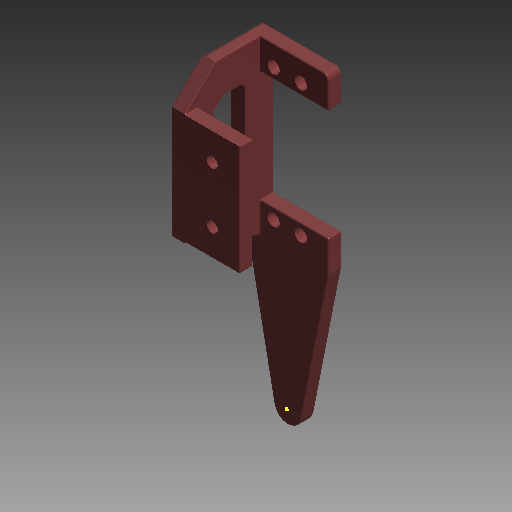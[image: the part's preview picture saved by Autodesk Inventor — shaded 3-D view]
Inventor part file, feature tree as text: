
AUTODESK INVENTOR PART (.ipt)
format: ipt  version: 2017 (Build 210142000, 142)  size: 246,272 bytes
history: native  units: mm (DEFAULTED — no unit token found)
features: other x3, sketch x1
ambient origin geometry x8: Origin, YZ Plane, XZ Plane, XY Plane, X Axis, Y Axis, Z Axis, Center Point
bodies: Solid1 (feature_tree)
feature tree (4):
  other  "Lower_leg_right.ipt"
  other  "Solid1::Lower_leg_right.ipt"
  other  "TaggingFeature1"
  sketch  "Sketch1"  dims[d0=10.0mm]
